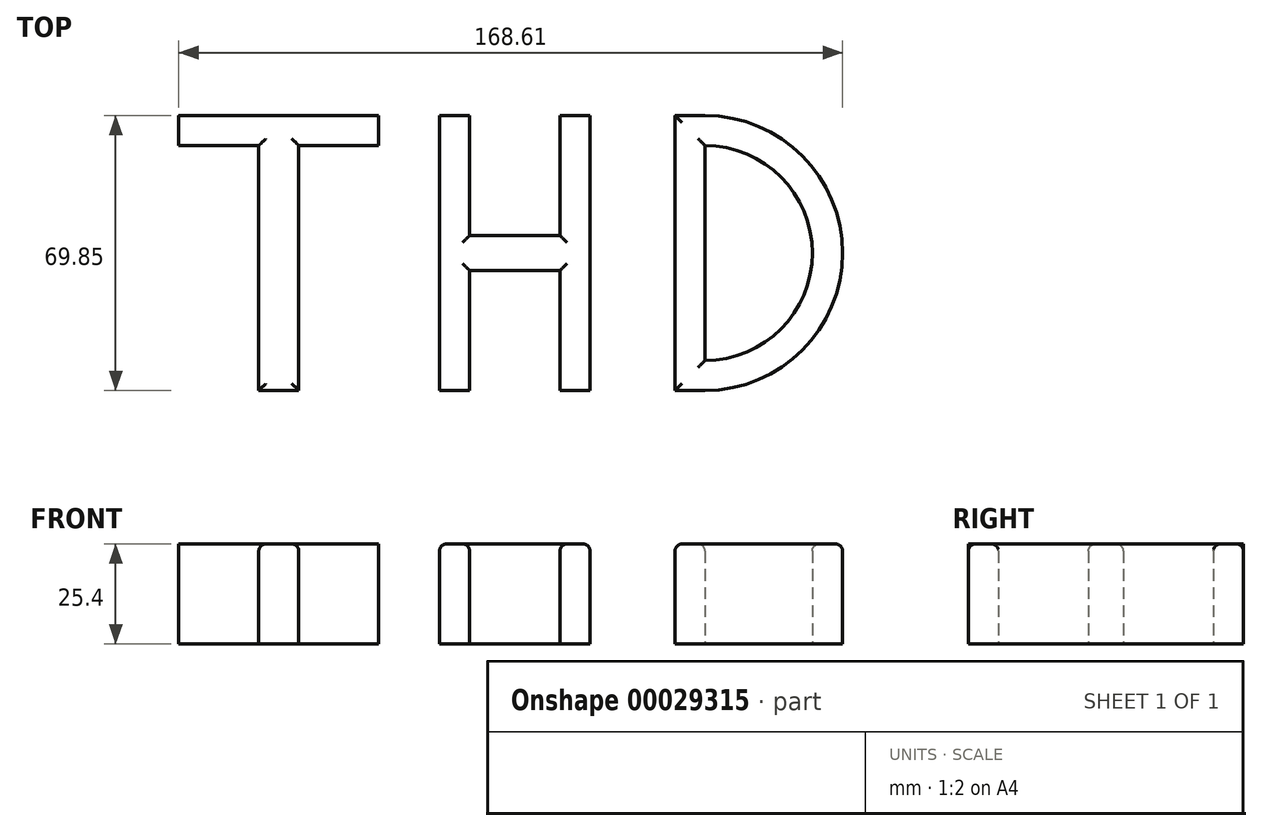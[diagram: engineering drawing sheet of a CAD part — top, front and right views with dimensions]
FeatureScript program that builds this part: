
annotation { "Feature Type Name" : "Feature", "Feature Type Description" : "" }
export const myFeature = defineFeature(function(context is Context, id is Id, definition is map)
    precondition{}
    {
        {
            var Q0;
            Q0=qCreatedBy(makeId("Top.planeOp"),FACE);
            var sketch = newSketch(context, id + "F0", { "sketchPlane" : qUnion([Q0])});
            skLineSegment(sketch, "E0", {"start": v(-106.65, -62.23) * mm, "end": v(103.47, -62.23) * mm, "construction": true});
            skLineSegment(sketch, "E1", {"start": v(-75.58, -62.23) * mm, "end": v(-75.58, 0) * mm});
            skLineSegment(sketch, "E2", {"start": v(-75.58, 0) * mm, "end": v(-55.26, 0) * mm});
            skLineSegment(sketch, "E3", {"start": v(-55.26, 0) * mm, "end": v(-55.26, 7.62) * mm});
            skLineSegment(sketch, "E4", {"start": v(-55.26, 7.62) * mm, "end": v(-106.06, 7.62) * mm});
            skLineSegment(sketch, "E5", {"start": v(-106.06, 7.62) * mm, "end": v(-106.06, 0) * mm});
            skLineSegment(sketch, "E6", {"start": v(-106.06, 0) * mm, "end": v(-85.74, 0) * mm});
            skLineSegment(sketch, "E7", {"start": v(-85.74, 0) * mm, "end": v(-85.74, -62.23) * mm});
            skLineSegment(sketch, "E8", {"start": v(-85.74, -62.23) * mm, "end": v(-75.58, -62.23) * mm});
            skLineSegment(sketch, "E9", {"start": v(-39.8, 7.62) * mm, "end": v(-39.8, -62.23) * mm});
            skLineSegment(sketch, "E10", {"start": v(-39.8, -62.23) * mm, "end": v(-32.19, -62.23) * mm});
            skLineSegment(sketch, "E11", {"start": v(-32.19, -62.23) * mm, "end": v(-32.19, -31.75) * mm});
            skLineSegment(sketch, "E12", {"start": v(-32.19, -31.75) * mm, "end": v(-9.2, -31.75) * mm});
            skLineSegment(sketch, "E13", {"start": v(-9.2, -31.75) * mm, "end": v(-9.2, -62.23) * mm});
            skLineSegment(sketch, "E14", {"start": v(-9.2, -62.23) * mm, "end": v(-1.59, -62.23) * mm});
            skLineSegment(sketch, "E15", {"start": v(-1.59, -62.23) * mm, "end": v(-1.59, 7.62) * mm});
            skLineSegment(sketch, "E16", {"start": v(-1.59, 7.62) * mm, "end": v(-9.2, 7.62) * mm});
            skLineSegment(sketch, "E17", {"start": v(-9.2, 7.62) * mm, "end": v(-9.2, -22.86) * mm});
            skLineSegment(sketch, "E18", {"start": v(-9.2, -22.86) * mm, "end": v(-32.19, -22.86) * mm});
            skLineSegment(sketch, "E19", {"start": v(-32.19, -22.86) * mm, "end": v(-32.19, 7.62) * mm});
            skLineSegment(sketch, "E20", {"start": v(-32.19, 7.62) * mm, "end": v(-39.8, 7.62) * mm});
            skLineSegment(sketch, "E21", {"start": v(20, 7.62) * mm, "end": v(20, -62.23) * mm});
            skLineSegment(sketch, "E22", {"start": v(20, -62.23) * mm, "end": v(27.63, -62.23) * mm});
            skLineSegment(sketch, "E23", {"start": v(27.63, -62.23) * mm, "end": v(27.63, 7.62) * mm});
            skLineSegment(sketch, "E24", {"start": v(27.63, 7.62) * mm, "end": v(20, 7.62) * mm});
            skArc(sketch, "E25", {"start": v(27.63, -62.23) * mm, "mid": v(62.55, -27.3) * mm, "end": v(27.63, 7.62) * mm});
            skPoint(sketch, "E26.end.orphan", {"position": v(27.63, 0) * mm});
            skPoint(sketch, "E26.start.orphan", {"position": v(27.63, -54.6) * mm});
            skArc(sketch, "E27", {"start": v(27.63, -54.6) * mm, "mid": v(54.88, -27.3) * mm, "end": v(27.63, 0) * mm});
            skSolve(sketch);
        }
        {
            var Q0;
            Q0 = qSketchRegion(id + "F0", true);
            extrude(context, id + "F1", {"entities" : qUnion([Q0]), "depth" : 25.4 * mm});
        }
        {
            var Q0;
            Q0=makeQuery(id+"F1.opExtrude","CAP_EDGE",EDGE,{"disambiguationData":[OSD([sQuery(id+"F0.wireOp",EDGE,"E8")])],"isStart":false});
            var Q1;
            Q1=makeQuery(id+"F1.opExtrude","CAP_EDGE",EDGE,{"disambiguationData":[OSD([sQuery(id+"F0.wireOp",EDGE,"E1")])],"isStart":false});
            var Q2;
            Q2=makeQuery(id+"F1.opExtrude","CAP_EDGE",EDGE,{"disambiguationData":[OSD([sQuery(id+"F0.wireOp",EDGE,"E7")])],"isStart":false});
            var Q3;
            Q3=makeQuery(id+"F1.opExtrude","CAP_EDGE",EDGE,{"disambiguationData":[OSD([sQuery(id+"F0.wireOp",EDGE,"E6")])],"isStart":false});
            var Q4;
            Q4=makeQuery(id+"F1.opExtrude","CAP_EDGE",EDGE,{"disambiguationData":[OSD([sQuery(id+"F0.wireOp",EDGE,"E2")])],"isStart":false});
            var Q5;
            Q5=makeQuery(id+"F1.opExtrude","CAP_EDGE",EDGE,{"disambiguationData":[OSD([sQuery(id+"F0.wireOp",EDGE,"E4")])],"isStart":false});
            var Q6;
            Q6=makeQuery(id+"F1.opExtrude","CAP_EDGE",EDGE,{"disambiguationData":[OSD([sQuery(id+"F0.wireOp",EDGE,"E11")])],"isStart":false});
            var Q7;
            Q7=makeQuery(id+"F1.opExtrude","CAP_EDGE",EDGE,{"disambiguationData":[OSD([sQuery(id+"F0.wireOp",EDGE,"E9")])],"isStart":false});
            var Q8;
            Q8=makeQuery(id+"F1.opExtrude","CAP_EDGE",EDGE,{"disambiguationData":[OSD([sQuery(id+"F0.wireOp",EDGE,"E19")])],"isStart":false});
            var Q9;
            Q9=makeQuery(id+"F1.opExtrude","CAP_EDGE",EDGE,{"disambiguationData":[OSD([sQuery(id+"F0.wireOp",EDGE,"E12")])],"isStart":false});
            var Q10;
            Q10=makeQuery(id+"F1.opExtrude","CAP_EDGE",EDGE,{"disambiguationData":[OSD([sQuery(id+"F0.wireOp",EDGE,"E18")])],"isStart":false});
            var Q11;
            Q11=makeQuery(id+"F1.opExtrude","CAP_EDGE",EDGE,{"disambiguationData":[OSD([sQuery(id+"F0.wireOp",EDGE,"E17")])],"isStart":false});
            var Q12;
            Q12=makeQuery(id+"F1.opExtrude","CAP_EDGE",EDGE,{"disambiguationData":[OSD([sQuery(id+"F0.wireOp",EDGE,"E13")])],"isStart":false});
            var Q13;
            Q13=makeQuery(id+"F1.opExtrude","CAP_EDGE",EDGE,{"disambiguationData":[OSD([sQuery(id+"F0.wireOp",EDGE,"E15")])],"isStart":false});
            var Q14;
            Q14=makeQuery(id+"F1.opExtrude","CAP_EDGE",EDGE,{"disambiguationData":[OSD([sQuery(id+"F0.wireOp",EDGE,"E21")])],"isStart":false});
            var Q15;
            Q15=makeQuery(id+"F1.opExtrude","CAP_EDGE",EDGE,{"disambiguationData":[OSD([sQuery(id+"F0.wireOp",EDGE,"E23")])],"isStart":false});
            var Q16;
            Q16=makeQuery(id+"F1.opExtrude","CAP_EDGE",EDGE,{"disambiguationData":[OSD([sQuery(id+"F0.wireOp",EDGE,"E25")])],"isStart":false});
            var Q17;
            Q17=makeQuery(id+"F1.opExtrude","CAP_EDGE",EDGE,{"disambiguationData":[OSD([sQuery(id+"F0.wireOp",EDGE,"E27")])],"isStart":false});
            var Q18;
            Q18=makeQuery(id+"F1.opExtrude","CAP_EDGE",EDGE,{"disambiguationData":[OSD([sQuery(id+"F0.wireOp",EDGE,"E24")])],"isStart":false});
            var Q19;
            Q19=makeQuery(id+"F1.opExtrude","CAP_EDGE",EDGE,{"disambiguationData":[OSD([sQuery(id+"F0.wireOp",EDGE,"E22")])],"isStart":false});
            fillet(context, id + "F2", {"entities" : qUnion([Q0, Q1, Q2, Q3, Q4, Q5, Q6, Q7, Q8, Q9, Q10, Q11, Q12, Q13, Q14, Q15, Q16, Q17, Q18, Q19]), "radius" : 1.78 * mm, "tangentPropagation" : true, "allowEdgeOverflow" : false});
        }
    });
